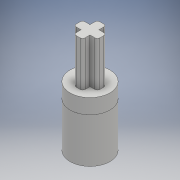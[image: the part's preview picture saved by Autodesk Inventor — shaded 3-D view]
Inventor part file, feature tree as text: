
AUTODESK INVENTOR PART (.ipt)
format: ipt  version: 2018.2 (Build 222227000, 227)  size: 153,088 bytes
history: native  units: mm
features: sketch x4, fillet x4, extrude x3
ambient origin geometry x8: Origin, YZ Plane, XZ Plane, XY Plane, X Axis, Y Axis, Z Axis, Center Point
bodies: Solid1 (feature_tree)
feature tree (11):
  extrude  "Extrusion1"  Depth=8.0mm
  extrude  "Extrusion2"  Depth=3.0mm TaperAngle=0.0deg
  extrude  "Extrusion3"  Depth=1.8mm
  sketch  "Sketch4"  dims[d14=9.0mm d15=0.0mm d19=0.5mm d20=0.5mm d21=0.5mm d22=0.5mm]
  fillet  "Fillet1"  Radius=2.4mm
  fillet  "Fillet2"  Radius=1.8mm
  fillet  "Fillet3"  Radius=4.8mm
  fillet  "Fillet4"  Radius=2.4mm
  sketch  "Sketch1"  dims[d0=4.25mm d1=8.0mm]
  sketch  "Sketch2"  dims[d2=9.0mm d3=0.0mm d4=3.0mm d5=0.0mm]
  sketch  "Sketch3"  dims[d6=4.8mm d7=1.8mm d8=2.4mm d10=1.8mm d11=4.8mm d12=2.4mm]
